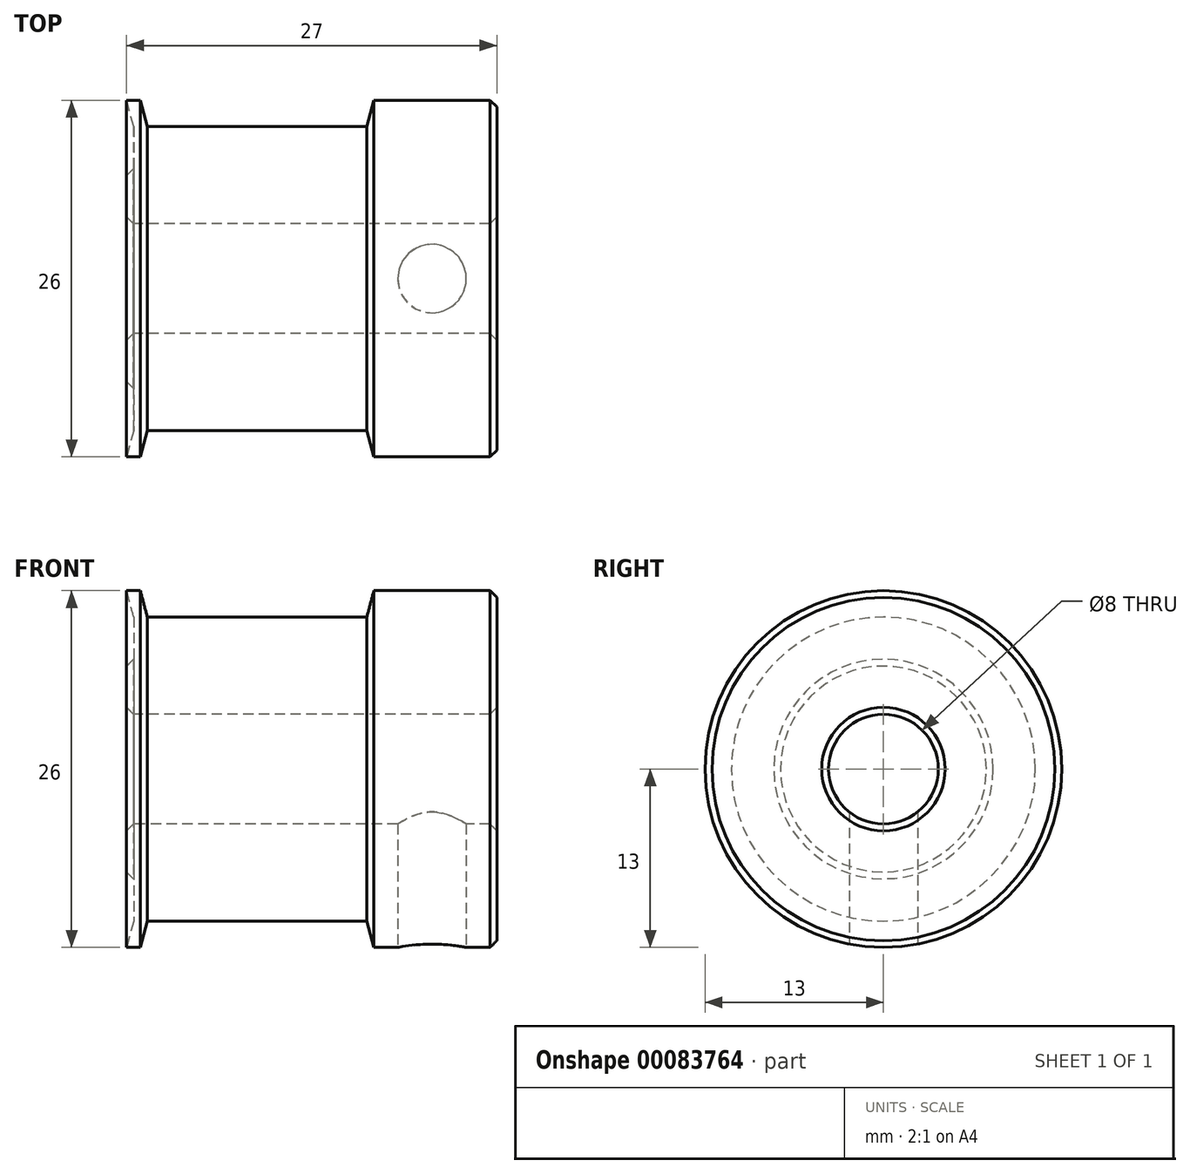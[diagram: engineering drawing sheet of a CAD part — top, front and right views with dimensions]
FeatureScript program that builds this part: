
annotation { "Feature Type Name" : "Feature", "Feature Type Description" : "" }
export const myFeature = defineFeature(function(context is Context, id is Id, definition is map)
    precondition{}
    {
        {
            var Q0;
            Q0=qCreatedBy(makeId("Front.planeOp"),FACE);
            var sketch = newSketch(context, id + "F0", { "sketchPlane" : qUnion([Q0])});
            skLineSegment(sketch, "E0", {"start": v(-9.49, 11.08) * mm, "end": v(-8.97, 13) * mm});
            skLineSegment(sketch, "E1", {"start": v(-8.97, 13) * mm, "end": v(0, 13) * mm});
            skLineSegment(sketch, "E2", {"start": v(-9.49, 11.08) * mm, "end": v(-25.49, 11.08) * mm});
            skLineSegment(sketch, "E3", {"start": v(-25.49, 11.08) * mm, "end": v(-26, 13) * mm});
            skLineSegment(sketch, "E4", {"start": v(-26, 13) * mm, "end": v(-27, 13) * mm});
            skLineSegment(sketch, "E5", {"start": v(-27, 13) * mm, "end": v(-26.49, 11.08) * mm});
            skLineSegment(sketch, "E6", {"start": v(-27, 0) * mm, "end": v(0, 0) * mm, "construction": true});
            skLineSegment(sketch, "E7", {"start": v(-27, 4) * mm, "end": v(0, 4) * mm});
            skLineSegment(sketch, "E8", {"start": v(0, 13) * mm, "end": v(0, 4) * mm});
            skLineSegment(sketch, "E9", {"start": v(-27, 4) * mm, "end": v(-27, 8) * mm});
            skLineSegment(sketch, "E10", {"start": v(-27, 8) * mm, "end": v(-26.49, 8) * mm});
            skLineSegment(sketch, "E11", {"start": v(-26.49, 8) * mm, "end": v(-26.49, 11.08) * mm});
            skSolve(sketch);
        }
        {
            var Q0;
            Q0 = qSketchRegion(id + "F0", true);
            var Q1;
            Q1=sQuery(id+"F0.wireOp",EDGE,"E6");
            revolve(context, id + "F1", {"entities" : qUnion([Q0]), "axis" : qUnion([Q1]), "revolveType" : RevolveType.FULL});
        }
        {
            var Q0;
            Q0=makeQuery(id+"F1.opRevolve","SWEPT_EDGE",EDGE,{"disambiguationData":[OSD([sQuery(id+"F0.wireOp",EDGE,"E7"),sQuery(id+"F0.wireOp",EDGE,"E8")])]});
            var Q1;
            Q1=makeQuery(id+"F1.opRevolve","SWEPT_EDGE",EDGE,{"disambiguationData":[OSD([sQuery(id+"F0.wireOp",EDGE,"E7"),sQuery(id+"F0.wireOp",EDGE,"YSZRkI3c-3nbe-fHHL-AThV-uhf47ApfAlM0")])]});
            var Q2;
            Q2=makeQuery(id+"F1.opRevolve","SWEPT_EDGE",EDGE,{"disambiguationData":[OSD([sQuery(id+"F0.wireOp",EDGE,"E1"),sQuery(id+"F0.wireOp",EDGE,"E8")])]});
            var Q3;
            Q3=makeQuery(id+"F1.opRevolve","SWEPT_EDGE",EDGE,{"disambiguationData":[OSD([sQuery(id+"F0.wireOp",EDGE,"E9"),sQuery(id+"F0.wireOp",EDGE,"E10")])]});
            chamfer(context, id + "F2", {"entities" : qUnion([Q0, Q1, Q2, Q3]), "width" : 0.5 * mm, "tangentPropagation" : true});
        }
        {
            var Q0;
            Q0=qCreatedBy(makeId("Top.planeOp"),FACE);
            var sketch = newSketch(context, id + "F3", { "sketchPlane" : qUnion([Q0])});
            skPoint(sketch, "E12", {"position": v(-4.74, 0) * mm});
            skLineSegment(sketch, "E13.0", {"start": v(-8.97, -13) * mm, "end": v(-8.97, 13) * mm, "construction": true});
            skLineSegment(sketch, "E14.0", {"start": v(-0.5, -13) * mm, "end": v(-0.5, 13) * mm, "construction": true});
            skLineSegment(sketch, "E15", {"start": v(-0.5, 0) * mm, "end": v(-8.97, 0) * mm, "construction": true});
            skSolve(sketch);
        }
        {
            var Q0;
            Q0=sQuery(id+"F3.wireOp",VERTEX,"E12");
            var Q1;
            Q1=makeQuery(id+"F1.opRevolve","SWEPT_BODY",BODY,{"disambiguationData":[OSD([sQuery(id+"F0.wireOp",EDGE,"E0"),sQuery(id+"F0.wireOp",EDGE,"E1"),sQuery(id+"F0.wireOp",EDGE,"E2"),sQuery(id+"F0.wireOp",EDGE,"E3"),sQuery(id+"F0.wireOp",EDGE,"E4"),sQuery(id+"F0.wireOp",EDGE,"E5"),sQuery(id+"F0.wireOp",EDGE,"E7"),sQuery(id+"F0.wireOp",EDGE,"E8"),sQuery(id+"F0.wireOp",EDGE,"E9"),sQuery(id+"F0.wireOp",EDGE,"E10"),sQuery(id+"F0.wireOp",EDGE,"E11")])]});
            hole(context, id + "F4", {"style" : HoleStyle.SIMPLE, "endStyle" : HoleEndStyle.THROUGH, "holeDiameter" : 5 * mm, "locations" : qUnion([Q0]), "scope" : qUnion([Q1]), "isTappedThrough" : true});
        }
    });
